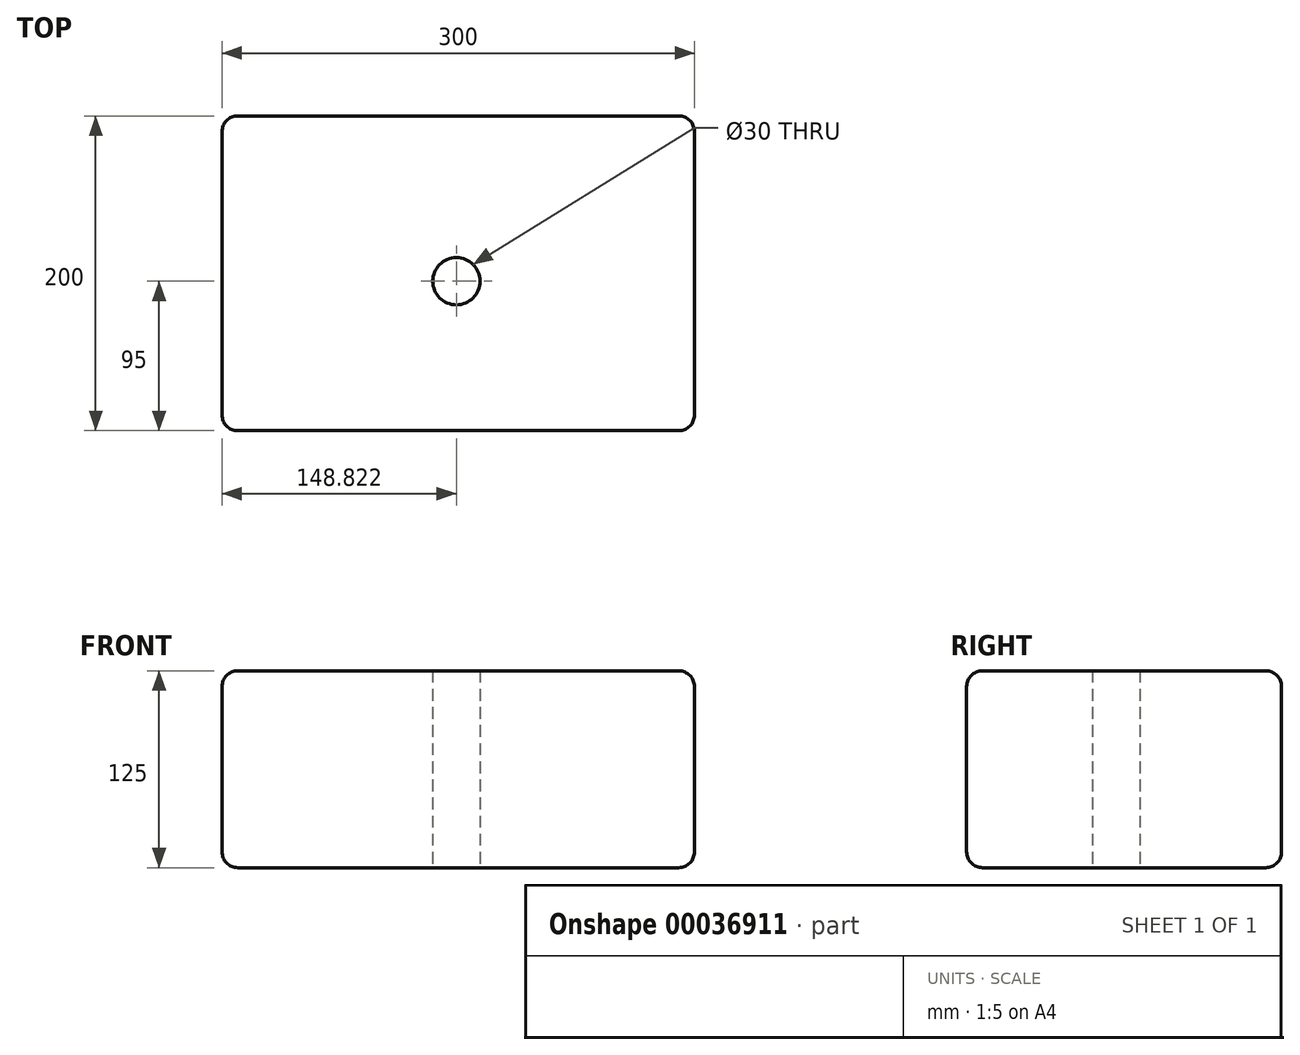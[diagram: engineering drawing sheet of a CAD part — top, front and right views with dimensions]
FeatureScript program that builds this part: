
annotation { "Feature Type Name" : "Feature", "Feature Type Description" : "" }
export const myFeature = defineFeature(function(context is Context, id is Id, definition is map)
    precondition{}
    {
        {
            var Q0;
            Q0=qCreatedBy(makeId("Top.planeOp"),FACE);
            var sketch = newSketch(context, id + "F0", { "sketchPlane" : qUnion([Q0])});
            skLineSegment(sketch, "E0.bottom", {"start": v(-150.74, 103.92) * mm, "end": v(149.26, 103.92) * mm});
            skLineSegment(sketch, "E0.top", {"start": v(-150.74, -96.08) * mm, "end": v(149.26, -96.08) * mm});
            skLineSegment(sketch, "E0.left", {"start": v(-150.74, 103.92) * mm, "end": v(-150.74, -96.08) * mm});
            skLineSegment(sketch, "E0.right", {"start": v(149.26, 103.92) * mm, "end": v(149.26, -96.08) * mm});
            skCircle(sketch, "E1", {"center": v(-1.92, -1.08) * mm, "radius": 15 * mm});
            skPoint(sketch, "E1.first.point", {"position": v(-11.77, 10.23) * mm});
            skPoint(sketch, "E1.second.point", {"position": v(10.26, -9.83) * mm});
            skPoint(sketch, "E1.third.point", {"position": v(6.87, 11.07) * mm});
            skSolve(sketch);
        }
        {
            var Q0;
            Q0=makeQuery(id+"F0.imprint","IMPRINT",FACE,{"disambiguationData":[TD([[makeQuery(id+"F0.imprint","IMPRINT",EDGE,{"derivedFrom":sQuery(id+"F0.wireOp",EDGE,"E0.bottom")}),-1.0]])]});
            extrude(context, id + "F1", {"entities" : qUnion([Q0]), "depth" : 25 * mm});
        }
        {
            var Q0;
            Q0 = qSketchRegion(id + "F0", true);
            extrude(context, id + "F2", {"entities" : qUnion([Q0]), "operationType" : NewBodyOperationType.ADD, "oppositeDirection" : true, "depth" : 100 * mm});
        }
        {
            var Q0;
            Q0=makeQuery(id+"F1.opExtrude","CAP_EDGE",EDGE,{"disambiguationData":[OSD([sQuery(id+"F0.wireOp",EDGE,"E0.left")])],"isStart":false});
            fillet(context, id + "F3", {"entities" : qUnion([Q0]), "radius" : 10 * mm, "tangentPropagation" : true, "allowEdgeOverflow" : false});
        }
        {
            var Q0;
            Q0=makeQuery(id+"F1.opExtrude","CAP_EDGE",EDGE,{"disambiguationData":[OSD([sQuery(id+"F0.wireOp",EDGE,"E0.right")])],"isStart":false});
            var Q1;
            Q1=makeQuery(id+"F2.opExtrude","CAP_EDGE",EDGE,{"disambiguationData":[OSD([sQuery(id+"F0.wireOp",EDGE,"E0.right")])],"isStart":false});
            var Q2;
            Q2=makeQuery(id+"F2.opExtrude","CAP_EDGE",EDGE,{"disambiguationData":[OSD([sQuery(id+"F0.wireOp",EDGE,"E0.top")])],"isStart":false});
            var Q3;
            {var subQ0=sQuery(id+"F0.wireOp",EDGE,"E0.top");var subQ1=sQuery(id+"F0.wireOp",EDGE,"E0.right");Q3=makeQuery(id+"F2.boolean.opBoolean","MERGE",EDGE,{"derivedFrom":[makeQuery(id+"F1.opExtrude","SWEPT_EDGE",EDGE,{"disambiguationData":[OSD([subQ0,subQ1])]}),makeQuery(id+"F2.opExtrude","SWEPT_EDGE",EDGE,{"disambiguationData":[OSD([subQ0,subQ1])]})]});}
            var Q4;
            Q4=makeQuery(id+"F2.opExtrude","CAP_EDGE",EDGE,{"disambiguationData":[OSD([sQuery(id+"F0.wireOp",EDGE,"E0.bottom")])],"isStart":false});
            var Q5;
            Q5=makeQuery(id+"F2.opExtrude","CAP_EDGE",EDGE,{"disambiguationData":[OSD([sQuery(id+"F0.wireOp",EDGE,"E0.left")])],"isStart":false});
            var Q6;
            {var subQ0=sQuery(id+"F0.wireOp",EDGE,"E0.bottom");var subQ1=sQuery(id+"F0.wireOp",EDGE,"E0.right");Q6=makeQuery(id+"F2.boolean.opBoolean","MERGE",EDGE,{"derivedFrom":[makeQuery(id+"F1.opExtrude","SWEPT_EDGE",EDGE,{"disambiguationData":[OSD([subQ0,subQ1])]}),makeQuery(id+"F2.opExtrude","SWEPT_EDGE",EDGE,{"disambiguationData":[OSD([subQ0,subQ1])]})]});}
            fillet(context, id + "F4", {"entities" : qUnion([Q0, Q1, Q2, Q3, Q4, Q5, Q6]), "radius" : 10 * mm, "tangentPropagation" : true, "allowEdgeOverflow" : false});
        }
        {
            var Q0;
            {var subQ0=sQuery(id+"F0.wireOp",EDGE,"E0.left");Q0=makeQuery(id+"F4.opFillet","BLEND_EDGE",EDGE,{"blendedFrom":[makeQuery(id+"F2.opExtrude","CAP_EDGE",EDGE,{"disambiguationData":[OSD([subQ0])],"isStart":false}),makeQuery(id+"F2.boolean.opBoolean","MERGE",FACE,{"derivedFrom":[makeQuery(id+"F1.opExtrude","SWEPT_FACE",FACE,{"disambiguationData":[OSD([subQ0])]}),makeQuery(id+"F2.opExtrude","SWEPT_FACE",FACE,{"disambiguationData":[OSD([subQ0])]})]})],"blendedInto":[makeQuery(id+"F2.boolean.opBoolean","MERGE",FACE,{"derivedFrom":[makeQuery(id+"F1.opExtrude","SWEPT_FACE",FACE,{"disambiguationData":[OSD([subQ0])]}),makeQuery(id+"F2.opExtrude","SWEPT_FACE",FACE,{"disambiguationData":[OSD([subQ0])]})]})]});}
            var Q1;
            {var subQ0=sQuery(id+"F0.wireOp",EDGE,"E0.top");Q1=makeQuery(id+"F4.opFillet","BLEND_EDGE",EDGE,{"blendedFrom":[makeQuery(id+"F2.opExtrude","CAP_EDGE",EDGE,{"disambiguationData":[OSD([subQ0])],"isStart":false}),makeQuery(id+"F2.boolean.opBoolean","MERGE",FACE,{"derivedFrom":[makeQuery(id+"F1.opExtrude","SWEPT_FACE",FACE,{"disambiguationData":[OSD([subQ0])]}),makeQuery(id+"F2.opExtrude","SWEPT_FACE",FACE,{"disambiguationData":[OSD([subQ0])]})]})],"blendedInto":[makeQuery(id+"F2.boolean.opBoolean","MERGE",FACE,{"derivedFrom":[makeQuery(id+"F1.opExtrude","SWEPT_FACE",FACE,{"disambiguationData":[OSD([subQ0])]}),makeQuery(id+"F2.opExtrude","SWEPT_FACE",FACE,{"disambiguationData":[OSD([subQ0])]})]})]});}
            var Q2;
            Q2=makeQuery(id+"F4.opFillet","BLEND_FACE",FACE,{"disambiguationData":[OSD([sQuery(id+"F0.wireOp",EDGE,"E0.bottom")])]});
            var Q3;
            {var subQ0=sQuery(id+"F0.wireOp",EDGE,"E0.bottom");Q3=makeQuery(id+"F4.opFillet","BLEND_EDGE",EDGE,{"blendedFrom":[makeQuery(id+"F2.opExtrude","CAP_EDGE",EDGE,{"disambiguationData":[OSD([subQ0])],"isStart":false}),makeQuery(id+"F2.boolean.opBoolean","MERGE",FACE,{"derivedFrom":[makeQuery(id+"F1.opExtrude","SWEPT_FACE",FACE,{"disambiguationData":[OSD([subQ0])]}),makeQuery(id+"F2.opExtrude","SWEPT_FACE",FACE,{"disambiguationData":[OSD([subQ0])]})]})],"blendedInto":[makeQuery(id+"F2.boolean.opBoolean","MERGE",FACE,{"derivedFrom":[makeQuery(id+"F1.opExtrude","SWEPT_FACE",FACE,{"disambiguationData":[OSD([subQ0])]}),makeQuery(id+"F2.opExtrude","SWEPT_FACE",FACE,{"disambiguationData":[OSD([subQ0])]})]})]});}
            fillet(context, id + "F5", {"entities" : qUnion([Q0, Q1, Q2, Q3]), "radius" : 10 * mm, "tangentPropagation" : true, "allowEdgeOverflow" : false});
        }
        {
            var Q0;
            {var subQ0=sQuery(id+"F0.wireOp",EDGE,"E0.top");var subQ1=sQuery(id+"F0.wireOp",EDGE,"E0.left");Q0=makeQuery(id+"F2.boolean.opBoolean","MERGE",EDGE,{"derivedFrom":[makeQuery(id+"F1.opExtrude","SWEPT_EDGE",EDGE,{"disambiguationData":[OSD([subQ0,subQ1])]}),makeQuery(id+"F2.opExtrude","SWEPT_EDGE",EDGE,{"disambiguationData":[OSD([subQ0,subQ1])]})]});}
            var Q1;
            Q1=makeQuery(id+"F4.opFillet","BLEND_EDGE",EDGE,{"blendedFrom":[makeQuery(id+"F2.opExtrude","CAP_EDGE",EDGE,{"disambiguationData":[OSD([sQuery(id+"F0.wireOp",EDGE,"E0.top")])],"isStart":false}),makeQuery(id+"F2.opExtrude","CAP_EDGE",EDGE,{"disambiguationData":[OSD([sQuery(id+"F0.wireOp",EDGE,"E0.left")])],"isStart":false})],"blendedInto":[]});
            fillet(context, id + "F6", {"entities" : qUnion([Q0, Q1]), "radius" : 10 * mm, "tangentPropagation" : true, "allowEdgeOverflow" : false});
        }
    });
